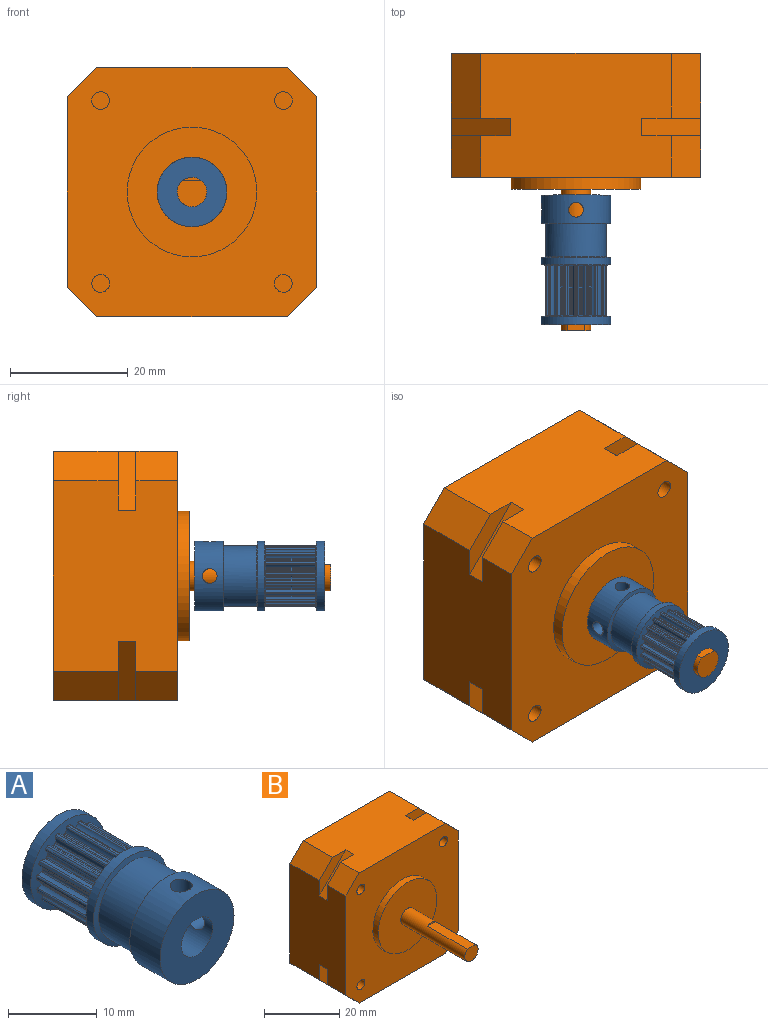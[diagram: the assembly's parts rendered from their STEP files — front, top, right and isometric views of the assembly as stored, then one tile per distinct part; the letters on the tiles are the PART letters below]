
ASSEMBLY  parts=2 mates=1
PART A: 149 faces, bbox 11.8x22x11.8 mm
  f0: cylinder r=5.9mm len=11.79mm, axis (0,1,0), area 168mm2, adj f20,f143,f144,f145
  f1: cylinder r=2.5mm len=22mm, axis (0,1,0), area 335.4mm2, adj f20,f21,f143,f144
  f2: cylinder r=5.16mm len=10.31mm, axis (0,-1,0), area 181.5mm2, adj f145,f147
  f3: cylinder r=5.16mm len=8.6mm, axis (0,-1,0), area 2.5mm2, adj f29,f30,f146,f148
  f4: cylinder r=5.16mm len=8.6mm, axis (0,-1,0), area 2.5mm2, adj f23,f141,f146,f148
  f5: cylinder r=5.16mm len=8.6mm, axis (0,-1,0), area 2.5mm2, adj f134,f135,f146,f148
  f6: cylinder r=5.16mm len=8.6mm, axis (0,-1,0), area 2.5mm2, adj f127,f128,f146,f148
  f7: cylinder r=5.16mm len=8.6mm, axis (0,-1,0), area 2.5mm2, adj f120,f121,f146,f148
  f8: cylinder r=5.16mm len=8.6mm, axis (0,-1,0), area 2.5mm2, adj f113,f114,f146,f148
  f9: cylinder r=5.16mm len=8.6mm, axis (0,-1,0), area 2.5mm2, adj f106,f107,f146,f148
  f10: cylinder r=5.16mm len=8.6mm, axis (0,-1,0), area 2.5mm2, adj f99,f100,f146,f148
  f11: cylinder r=5.16mm len=8.6mm, axis (0,-1,0), area 2.5mm2, adj f92,f93,f146,f148
  f12: cylinder r=5.16mm len=8.6mm, axis (0,-1,0), area 2.5mm2, adj f85,f86,f146,f148
  f13: cylinder r=5.16mm len=8.6mm, axis (0,-1,0), area 2.5mm2, adj f78,f79,f146,f148
  f14: cylinder r=5.16mm len=8.6mm, axis (0,-1,0), area 2.5mm2, adj f71,f72,f146,f148
  f15: cylinder r=5.16mm len=8.6mm, axis (0,-1,0), area 2.5mm2, adj f64,f65,f146,f148
  f16: cylinder r=5.16mm len=8.6mm, axis (0,-1,0), area 2.5mm2, adj f57,f58,f146,f148
  f17: cylinder r=5.16mm len=8.6mm, axis (0,-1,0), area 2.5mm2, adj f50,f51,f146,f148
  f18: cylinder r=5.16mm len=8.6mm, axis (0,-1,0), area 2.5mm2, adj f43,f44,f146,f148
  f19: cylinder r=5.9mm len=11.79mm, axis (0,1,0), area 51.9mm2, adj f21,f148
  f20: plane 11.79x11.79mm, normal (0,-1,0), area 89.6mm2, adj f0,f1
  f21: plane 11.79x11.79mm, normal (0,1,0), area 89.6mm2, adj f1,f19
  f22: cylinder r=5.16mm len=8.6mm, axis (0,-1,0), area 2.5mm2, adj f36,f37,f146,f148
  f23: cylinder r=0.2mm len=8.6mm, axis (0,-1,0), area 2.4mm2, adj f4,f24,f146,f148
  f24: cylinder r=1.3mm len=8.56mm, axis (0,-1,0), area 5.1mm2, adj f23,f25,f146,f148
  f25: cylinder r=0.2mm len=8.42mm, axis (0,-1,0), area 1.4mm2, adj f24,f26,f146,f148
  f26: cylinder r=4.4mm len=8.4mm, axis (0,-1,0), area 2.1mm2, adj f25,f27,f146,f148
  f27: cylinder r=0.2mm len=8.42mm, axis (0,-1,0), area 1.4mm2, adj f26,f28,f146,f148
  f28: cylinder r=1.3mm len=8.56mm, axis (0,-1,0), area 5.1mm2, adj f27,f29,f146,f148
  f29: cylinder r=0.2mm len=8.6mm, axis (0,-1,0), area 2.4mm2, adj f3,f28,f146,f148
  f30: cylinder r=0.2mm len=8.6mm, axis (0,-1,0), area 2.4mm2, adj f3,f31,f146,f148
  f31: cylinder r=1.3mm len=8.56mm, axis (0,-1,0), area 5.1mm2, adj f30,f32,f146,f148
  f32: cylinder r=0.2mm len=8.42mm, axis (0,-1,0), area 1.4mm2, adj f31,f33,f146,f148
  f33: cylinder r=4.4mm len=8.4mm, axis (0,-1,0), area 2.1mm2, adj f32,f34,f146,f148
  f34: cylinder r=0.2mm len=8.42mm, axis (0,-1,0), area 1.4mm2, adj f33,f35,f146,f148
  f35: cylinder r=1.3mm len=8.56mm, axis (0,-1,0), area 5.1mm2, adj f34,f36,f146,f148
  f36: cylinder r=0.2mm len=8.6mm, axis (0,-1,0), area 2.4mm2, adj f22,f35,f146,f148
  f37: cylinder r=0.2mm len=8.6mm, axis (0,-1,0), area 2.4mm2, adj f22,f38,f146,f148
  f38: cylinder r=1.3mm len=8.56mm, axis (0,-1,0), area 5.1mm2, adj f37,f39,f146,f148
  f39: cylinder r=0.2mm len=8.42mm, axis (0,-1,0), area 1.4mm2, adj f38,f40,f146,f148
  f40: cylinder r=4.4mm len=8.4mm, axis (0,-1,0), area 2.1mm2, adj f39,f41,f146,f148
  f41: cylinder r=0.2mm len=8.42mm, axis (0,-1,0), area 1.4mm2, adj f40,f42,f146,f148
  f42: cylinder r=1.3mm len=8.56mm, axis (0,-1,0), area 5.1mm2, adj f41,f43,f146,f148
  f43: cylinder r=0.2mm len=8.6mm, axis (0,-1,0), area 2.4mm2, adj f18,f42,f146,f148
  f44: cylinder r=0.2mm len=8.6mm, axis (0,-1,0), area 2.4mm2, adj f18,f45,f146,f148
  f45: cylinder r=1.3mm len=8.56mm, axis (0,-1,0), area 5.1mm2, adj f44,f46,f146,f148
  f46: cylinder r=0.2mm len=8.42mm, axis (0,-1,0), area 1.4mm2, adj f45,f47,f146,f148
  f47: cylinder r=4.4mm len=8.4mm, axis (0,-1,0), area 2.1mm2, adj f46,f48,f146,f148
  f48: cylinder r=0.2mm len=8.42mm, axis (0,-1,0), area 1.4mm2, adj f47,f49,f146,f148
  f49: cylinder r=1.3mm len=8.56mm, axis (0,-1,0), area 5.1mm2, adj f48,f50,f146,f148
  f50: cylinder r=0.2mm len=8.6mm, axis (0,-1,0), area 2.4mm2, adj f17,f49,f146,f148
  f51: cylinder r=0.2mm len=8.6mm, axis (0,-1,0), area 2.4mm2, adj f17,f52,f146,f148
  f52: cylinder r=1.3mm len=8.56mm, axis (0,-1,0), area 5.1mm2, adj f51,f53,f146,f148
  f53: cylinder r=0.2mm len=8.42mm, axis (0,-1,0), area 1.4mm2, adj f52,f54,f146,f148
  f54: cylinder r=4.4mm len=8.4mm, axis (0,-1,0), area 2.1mm2, adj f53,f55,f146,f148
  f55: cylinder r=0.2mm len=8.42mm, axis (0,-1,0), area 1.4mm2, adj f54,f56,f146,f148
  f56: cylinder r=1.3mm len=8.56mm, axis (0,-1,0), area 5.1mm2, adj f55,f57,f146,f148
  f57: cylinder r=0.2mm len=8.6mm, axis (0,-1,0), area 2.4mm2, adj f16,f56,f146,f148
  f58: cylinder r=0.2mm len=8.6mm, axis (0,-1,0), area 2.4mm2, adj f16,f59,f146,f148
  f59: cylinder r=1.3mm len=8.56mm, axis (0,-1,0), area 5.1mm2, adj f58,f60,f146,f148
  f60: cylinder r=0.2mm len=8.42mm, axis (0,-1,0), area 1.4mm2, adj f59,f61,f146,f148
  f61: cylinder r=4.4mm len=8.4mm, axis (0,-1,0), area 2.1mm2, adj f60,f62,f146,f148
  f62: cylinder r=0.2mm len=8.42mm, axis (0,-1,0), area 1.4mm2, adj f61,f63,f146,f148
  f63: cylinder r=1.3mm len=8.56mm, axis (0,-1,0), area 5.1mm2, adj f62,f64,f146,f148
  f64: cylinder r=0.2mm len=8.6mm, axis (0,-1,0), area 2.4mm2, adj f15,f63,f146,f148
  f65: cylinder r=0.2mm len=8.6mm, axis (0,-1,0), area 2.4mm2, adj f15,f66,f146,f148
  f66: cylinder r=1.3mm len=8.56mm, axis (0,-1,0), area 5.1mm2, adj f65,f67,f146,f148
  f67: cylinder r=0.2mm len=8.42mm, axis (0,-1,0), area 1.4mm2, adj f66,f68,f146,f148
  f68: cylinder r=4.4mm len=8.4mm, axis (0,-1,0), area 2.1mm2, adj f67,f69,f146,f148
  f69: cylinder r=0.2mm len=8.42mm, axis (0,-1,0), area 1.4mm2, adj f68,f70,f146,f148
  f70: cylinder r=1.3mm len=8.56mm, axis (0,-1,0), area 5.1mm2, adj f69,f71,f146,f148
  f71: cylinder r=0.2mm len=8.6mm, axis (0,-1,0), area 2.4mm2, adj f14,f70,f146,f148
  f72: cylinder r=0.2mm len=8.6mm, axis (0,-1,0), area 2.4mm2, adj f14,f73,f146,f148
  f73: cylinder r=1.3mm len=8.56mm, axis (0,-1,0), area 5.1mm2, adj f72,f74,f146,f148
  f74: cylinder r=0.2mm len=8.42mm, axis (0,-1,0), area 1.4mm2, adj f73,f75,f146,f148
  f75: cylinder r=4.4mm len=8.4mm, axis (0,-1,0), area 2.1mm2, adj f74,f76,f146,f148
  f76: cylinder r=0.2mm len=8.42mm, axis (0,-1,0), area 1.4mm2, adj f75,f77,f146,f148
  f77: cylinder r=1.3mm len=8.56mm, axis (0,-1,0), area 5.1mm2, adj f76,f78,f146,f148
  f78: cylinder r=0.2mm len=8.6mm, axis (0,-1,0), area 2.4mm2, adj f13,f77,f146,f148
  f79: cylinder r=0.2mm len=8.6mm, axis (0,-1,0), area 2.4mm2, adj f13,f80,f146,f148
  f80: cylinder r=1.3mm len=8.56mm, axis (0,-1,0), area 5.1mm2, adj f79,f81,f146,f148
  f81: cylinder r=0.2mm len=8.42mm, axis (0,-1,0), area 1.4mm2, adj f80,f82,f146,f148
  f82: cylinder r=4.4mm len=8.4mm, axis (0,-1,0), area 2.1mm2, adj f81,f83,f146,f148
  f83: cylinder r=0.2mm len=8.42mm, axis (0,-1,0), area 1.4mm2, adj f82,f84,f146,f148
  f84: cylinder r=1.3mm len=8.56mm, axis (0,-1,0), area 5.1mm2, adj f83,f85,f146,f148
  f85: cylinder r=0.2mm len=8.6mm, axis (0,-1,0), area 2.4mm2, adj f12,f84,f146,f148
  f86: cylinder r=0.2mm len=8.6mm, axis (0,-1,0), area 2.4mm2, adj f12,f87,f146,f148
  f87: cylinder r=1.3mm len=8.56mm, axis (0,-1,0), area 5.1mm2, adj f86,f88,f146,f148
  f88: cylinder r=0.2mm len=8.42mm, axis (0,-1,0), area 1.4mm2, adj f87,f89,f146,f148
  f89: cylinder r=4.4mm len=8.4mm, axis (0,-1,0), area 2.1mm2, adj f88,f90,f146,f148
  f90: cylinder r=0.2mm len=8.42mm, axis (0,-1,0), area 1.4mm2, adj f89,f91,f146,f148
  f91: cylinder r=1.3mm len=8.56mm, axis (0,-1,0), area 5.1mm2, adj f90,f92,f146,f148
  f92: cylinder r=0.2mm len=8.6mm, axis (0,-1,0), area 2.4mm2, adj f11,f91,f146,f148
  f93: cylinder r=0.2mm len=8.6mm, axis (0,-1,0), area 2.4mm2, adj f11,f94,f146,f148
  f94: cylinder r=1.3mm len=8.56mm, axis (0,-1,0), area 5.1mm2, adj f93,f95,f146,f148
  f95: cylinder r=0.2mm len=8.42mm, axis (0,-1,0), area 1.4mm2, adj f94,f96,f146,f148
  f96: cylinder r=4.4mm len=8.4mm, axis (0,-1,0), area 2.1mm2, adj f95,f97,f146,f148
  f97: cylinder r=0.2mm len=8.42mm, axis (0,-1,0), area 1.4mm2, adj f96,f98,f146,f148
  f98: cylinder r=1.3mm len=8.56mm, axis (0,-1,0), area 5.1mm2, adj f97,f99,f146,f148
  f99: cylinder r=0.2mm len=8.6mm, axis (0,-1,0), area 2.4mm2, adj f10,f98,f146,f148
  f100: cylinder r=0.2mm len=8.6mm, axis (0,-1,0), area 2.4mm2, adj f10,f101,f146,f148
  f101: cylinder r=1.3mm len=8.56mm, axis (0,-1,0), area 5.1mm2, adj f100,f102,f146,f148
  f102: cylinder r=0.2mm len=8.42mm, axis (0,-1,0), area 1.4mm2, adj f101,f103,f146,f148
  f103: cylinder r=4.4mm len=8.4mm, axis (0,-1,0), area 2.1mm2, adj f102,f104,f146,f148
  f104: cylinder r=0.2mm len=8.42mm, axis (0,-1,0), area 1.4mm2, adj f103,f105,f146,f148
  f105: cylinder r=1.3mm len=8.56mm, axis (0,-1,0), area 5.1mm2, adj f104,f106,f146,f148
  f106: cylinder r=0.2mm len=8.6mm, axis (0,-1,0), area 2.4mm2, adj f9,f105,f146,f148
  f107: cylinder r=0.2mm len=8.6mm, axis (0,-1,0), area 2.4mm2, adj f9,f108,f146,f148
  f108: cylinder r=1.3mm len=8.56mm, axis (0,-1,0), area 5.1mm2, adj f107,f109,f146,f148
  f109: cylinder r=0.2mm len=8.42mm, axis (0,-1,0), area 1.4mm2, adj f108,f110,f146,f148
  f110: cylinder r=4.4mm len=8.4mm, axis (0,-1,0), area 2.1mm2, adj f109,f111,f146,f148
  f111: cylinder r=0.2mm len=8.42mm, axis (0,-1,0), area 1.4mm2, adj f110,f112,f146,f148
  f112: cylinder r=1.3mm len=8.56mm, axis (0,-1,0), area 5.1mm2, adj f111,f113,f146,f148
  f113: cylinder r=0.2mm len=8.6mm, axis (0,-1,0), area 2.4mm2, adj f8,f112,f146,f148
  f114: cylinder r=0.2mm len=8.6mm, axis (0,-1,0), area 2.4mm2, adj f8,f115,f146,f148
  f115: cylinder r=1.3mm len=8.56mm, axis (0,-1,0), area 5.1mm2, adj f114,f116,f146,f148
  f116: cylinder r=0.2mm len=8.42mm, axis (0,-1,0), area 1.4mm2, adj f115,f117,f146,f148
  f117: cylinder r=4.4mm len=8.4mm, axis (0,-1,0), area 2.1mm2, adj f116,f118,f146,f148
  f118: cylinder r=0.2mm len=8.42mm, axis (0,-1,0), area 1.4mm2, adj f117,f119,f146,f148
  f119: cylinder r=1.3mm len=8.56mm, axis (0,-1,0), area 5.1mm2, adj f118,f120,f146,f148
  f120: cylinder r=0.2mm len=8.6mm, axis (0,-1,0), area 2.4mm2, adj f7,f119,f146,f148
  f121: cylinder r=0.2mm len=8.6mm, axis (0,-1,0), area 2.4mm2, adj f7,f122,f146,f148
  f122: cylinder r=1.3mm len=8.56mm, axis (0,-1,0), area 5.1mm2, adj f121,f123,f146,f148
  f123: cylinder r=0.2mm len=8.42mm, axis (0,-1,0), area 1.4mm2, adj f122,f124,f146,f148
  f124: cylinder r=4.4mm len=8.4mm, axis (0,-1,0), area 2.1mm2, adj f123,f125,f146,f148
  f125: cylinder r=0.2mm len=8.42mm, axis (0,-1,0), area 1.4mm2, adj f124,f126,f146,f148
  f126: cylinder r=1.3mm len=8.56mm, axis (0,-1,0), area 5.1mm2, adj f125,f127,f146,f148
  f127: cylinder r=0.2mm len=8.6mm, axis (0,-1,0), area 2.4mm2, adj f6,f126,f146,f148
  f128: cylinder r=0.2mm len=8.6mm, axis (0,-1,0), area 2.4mm2, adj f6,f129,f146,f148
  f129: cylinder r=1.3mm len=8.56mm, axis (0,-1,0), area 5.1mm2, adj f128,f130,f146,f148
  f130: cylinder r=0.2mm len=8.42mm, axis (0,-1,0), area 1.4mm2, adj f129,f131,f146,f148
  f131: cylinder r=4.4mm len=8.4mm, axis (0,-1,0), area 2.1mm2, adj f130,f132,f146,f148
  f132: cylinder r=0.2mm len=8.42mm, axis (0,-1,0), area 1.4mm2, adj f131,f133,f146,f148
  f133: cylinder r=1.3mm len=8.56mm, axis (0,-1,0), area 5.1mm2, adj f132,f134,f146,f148
  f134: cylinder r=0.2mm len=8.6mm, axis (0,-1,0), area 2.4mm2, adj f5,f133,f146,f148
  f135: cylinder r=0.2mm len=8.6mm, axis (0,-1,0), area 2.4mm2, adj f5,f136,f146,f148
  f136: cylinder r=1.3mm len=8.56mm, axis (0,-1,0), area 5.1mm2, adj f135,f137,f146,f148
  f137: cylinder r=0.2mm len=8.42mm, axis (0,-1,0), area 1.4mm2, adj f136,f138,f146,f148
  f138: cylinder r=4.4mm len=8.4mm, axis (0,-1,0), area 2.1mm2, adj f137,f139,f146,f148
  f139: cylinder r=0.2mm len=8.42mm, axis (0,-1,0), area 1.4mm2, adj f138,f140,f146,f148
  f140: cylinder r=1.3mm len=8.56mm, axis (0,-1,0), area 5.1mm2, adj f139,f141,f146,f148
  f141: cylinder r=0.2mm len=8.6mm, axis (0,-1,0), area 2.4mm2, adj f4,f140,f146,f148
  f142: cylinder r=5.9mm len=11.79mm, axis (0,1,0), area 44.5mm2, adj f146,f147
  f143: cylinder r=1.25mm len=3.73mm, axis (0,0,-1), area 27.5mm2, adj f0,f1
  f144: cylinder r=1.25mm len=3.73mm, axis (-1,0,0), area 27.4mm2, adj f0,f1
  f145: cone r=5.9mm half-angle=82.4deg, axis (0,-1,0), area 25.9mm2, adj f0,f2
  f146: cone r=5.9mm half-angle=82.4deg, axis (0,-1,0), area 38.4mm2, adj f3,f4,f5,f6,f7,f8,f9,f10
  f147: cone r=4.4mm half-angle=82.4deg, axis (0,1,0), area 25.9mm2, adj f2,f142
  f148: cone r=4.4mm half-angle=82.4deg, axis (0,1,0), area 38.4mm2, adj f3,f4,f5,f6,f7,f8,f9,f10
PART B: 48 faces, bbox 42.3x47x42.3 mm
  f0: plane 10x10mm, normal (0,-1,0), area 37.5mm2, adj f4,f5,f10,f21
  f1: plane 10x10mm, normal (0,-1,0), area 37.5mm2, adj f5,f6,f9,f22
  f2: plane 10x10mm, normal (0,-1,0), area 37.5mm2, adj f3,f6,f12,f23
  f3: plane 32.3x21mm, normal (1,0,0), area 648.3mm2, adj f2,f7,f8,f11,f12,f23,f24,f26
  f4: plane 32.3x21mm, normal (0,0,-1), area 648.3mm2, adj f0,f7,f8,f10,f11,f21,f24,f25
  f5: plane 32.3x21mm, normal (-1,0,0), area 648.3mm2, adj f0,f1,f7,f9,f10,f21,f22,f25
  f6: plane 32.3x21mm, normal (0,0,1), area 648.3mm2, adj f1,f2,f7,f9,f12,f22,f23,f27
  f7: plane 42.3x42.3mm, normal (0,1,0), area 1711mm2, adj f3,f4,f5,f6,f9,f10,f11,f12
  f8: plane 10x10mm, normal (0,-1,0), area 37.5mm2, adj f3,f4,f11,f24
  f9: plane 11x5mm, normal (-0.71,0,0.71), area 77.8mm2, adj f1,f5,f6,f7
  f10: plane 11x5mm, normal (-0.71,0,-0.71), area 77.8mm2, adj f0,f4,f5,f7
  f11: plane 11x5mm, normal (0.71,0,-0.71), area 77.8mm2, adj f3,f4,f7,f8
  f12: plane 11x5mm, normal (0.71,0,0.71), area 77.8mm2, adj f2,f3,f6,f7
  f13: cylinder r=1.5mm len=4.5mm, axis (0,1,0), area 42.4mm2, adj f7,f14
  f14: plane 3x3mm, normal (0,1,0), area 7.1mm2, adj f13
  f15: cylinder r=1.5mm len=4.5mm, axis (0,1,0), area 42.4mm2, adj f7,f16
  f16: plane 3x3mm, normal (0,1,0), area 7.1mm2, adj f15
  f17: cylinder r=1.5mm len=4.5mm, axis (0,1,0), area 42.4mm2, adj f7,f18
  f18: plane 3x3mm, normal (0,1,0), area 7.1mm2, adj f17
  f19: cylinder r=1.5mm len=4.5mm, axis (0,1,0), area 42.4mm2, adj f7,f20
  f20: plane 3x3mm, normal (0,1,0), area 7.1mm2, adj f19
  f21: plane 10x10mm, normal (-0.71,0,-0.71), area 42.4mm2, adj f0,f4,f5,f25
  f22: plane 10x10mm, normal (-0.71,0,0.71), area 42.4mm2, adj f1,f5,f6,f28
  f23: plane 10x10mm, normal (0.71,0,0.71), area 42.4mm2, adj f2,f3,f6,f27
  f24: plane 10x10mm, normal (0.71,0,-0.71), area 42.4mm2, adj f3,f4,f8,f26
  f25: plane 10x10mm, normal (0,1,0), area 37.5mm2, adj f4,f5,f21,f34
  f26: plane 10x10mm, normal (0,1,0), area 37.5mm2, adj f3,f4,f24,f35
  f27: plane 10x10mm, normal (0,1,0), area 37.5mm2, adj f3,f6,f23,f36
  f28: plane 10x10mm, normal (0,1,0), area 37.5mm2, adj f5,f6,f22,f37
  f29: cylinder r=2.5mm len=24mm, axis (0,1,0), area 328.7mm2, adj f30,f31,f32,f39
  f30: plane 5x4.5mm, normal (0,-1,0), area 18.6mm2, adj f29,f31
  f31: plane 15x3mm, normal (0,0,1), area 45mm2, adj f29,f30,f32
  f32: plane 3x0.5mm, normal (0,-1,0), area 1mm2, adj f29,f31
  f33: plane 42.3x42.3mm, normal (0,-1,0), area 1330.9mm2, adj f3,f4,f5,f6,f34,f35,f36,f37
  f34: plane 7x5mm, normal (-0.71,0,-0.71), area 49.5mm2, adj f4,f5,f25,f33
  f35: plane 7x5mm, normal (0.71,0,-0.71), area 49.5mm2, adj f3,f4,f26,f33
  f36: plane 7x5mm, normal (0.71,0,0.71), area 49.5mm2, adj f3,f6,f27,f33
  f37: plane 7x5mm, normal (-0.71,0,0.71), area 49.5mm2, adj f5,f6,f28,f33
  f38: cylinder r=11mm len=22mm, axis (0,1,0), area 138.2mm2, adj f33,f39
  f39: plane 22x22mm, normal (0,-1,0), area 360.5mm2, adj f29,f38
  f40: cylinder r=1.5mm len=4.5mm, axis (0,-1,0), area 42.4mm2, adj f33,f41
  f41: plane 3x3mm, normal (0,-1,0), area 7.1mm2, adj f40
  f42: cylinder r=1.5mm len=4.5mm, axis (0,-1,0), area 42.4mm2, adj f33,f43
  f43: plane 3x3mm, normal (0,-1,0), area 7.1mm2, adj f42
  f44: cylinder r=1.5mm len=4.5mm, axis (0,-1,0), area 42.4mm2, adj f33,f45
  f45: plane 3x3mm, normal (0,-1,0), area 7.1mm2, adj f44
  f46: cylinder r=1.5mm len=4.5mm, axis (0,-1,0), area 42.4mm2, adj f33,f47
  f47: plane 3x3mm, normal (0,-1,0), area 7.1mm2, adj f46
PLACE A rot(axis=(0,0,1),180deg) t=(-18.45,-22,13.43)mm
PLACE B at identity
MATE fastened A.f0 <-> B.f29  axis (0,-1,0) through (-18.45,-10,13.43)mm
